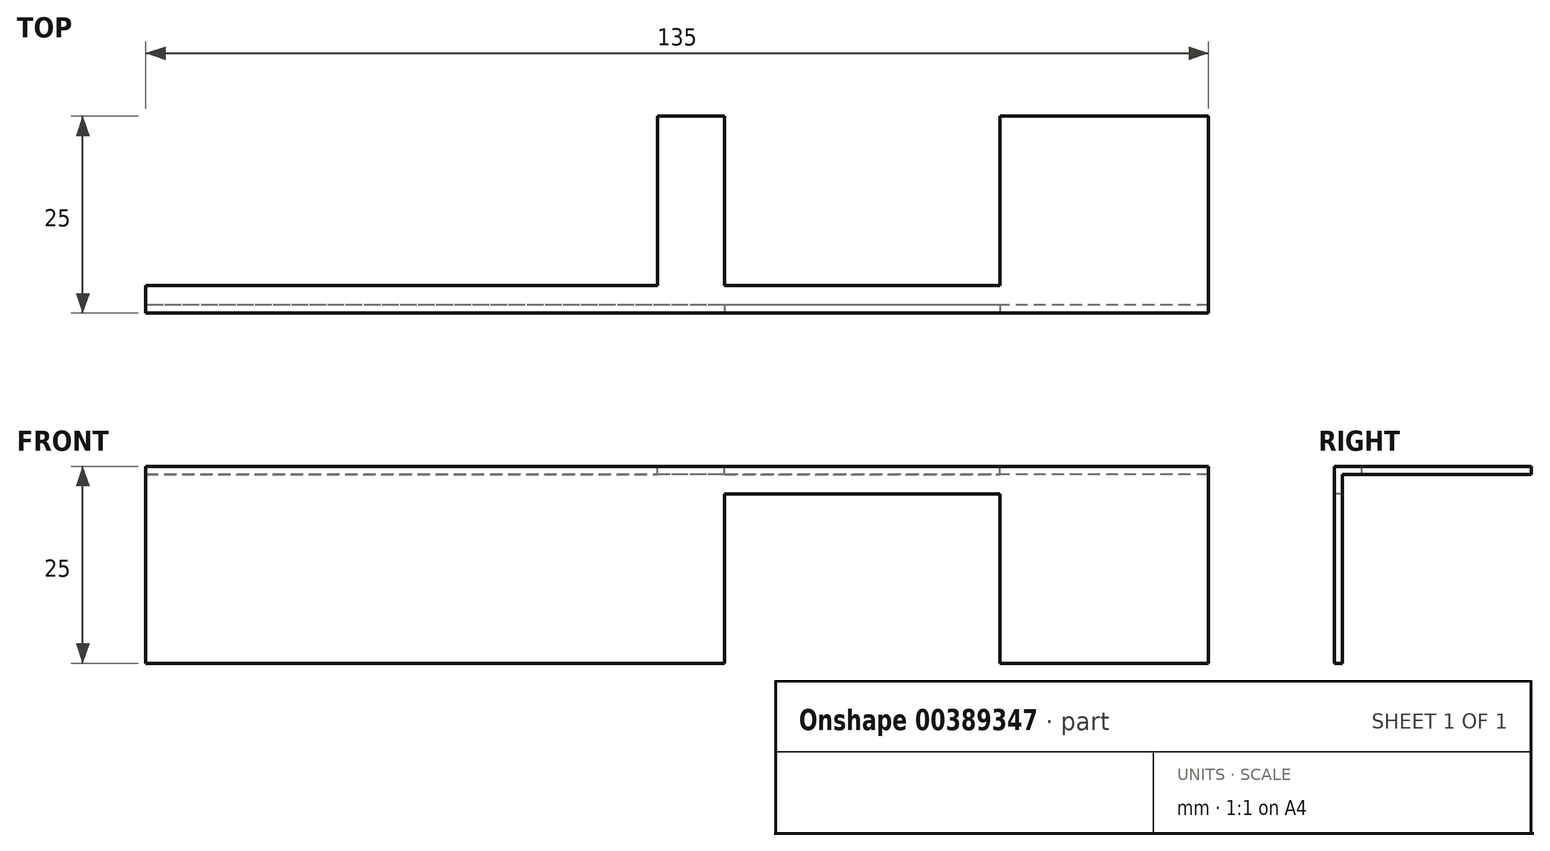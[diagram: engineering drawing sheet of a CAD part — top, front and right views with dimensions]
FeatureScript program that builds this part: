
annotation { "Feature Type Name" : "Feature", "Feature Type Description" : "" }
export const myFeature = defineFeature(function(context is Context, id is Id, definition is map)
    precondition{}
    {
        {
            var Q0;
            Q0=qCreatedBy(makeId("Right.planeOp"),FACE);
            var sketch = newSketch(context, id + "F0", { "sketchPlane" : qUnion([Q0])});
            skLineSegment(sketch, "E0.bottom", {"start": v(-65.04, 19.74) * mm, "end": v(-64.04, 19.74) * mm});
            skLineSegment(sketch, "E0.top", {"start": v(-65.04, 44.74) * mm, "end": v(-64.04, 44.74) * mm});
            skLineSegment(sketch, "E0.left", {"start": v(-65.04, 19.74) * mm, "end": v(-65.04, 44.74) * mm});
            skLineSegment(sketch, "E0.right", {"start": v(-64.04, 19.74) * mm, "end": v(-64.04, 44.74) * mm});
            skLineSegment(sketch, "E1.bottom", {"start": v(-65.04, 44.74) * mm, "end": v(-40.04, 44.74) * mm});
            skLineSegment(sketch, "E1.top", {"start": v(-65.04, 43.74) * mm, "end": v(-40.04, 43.74) * mm});
            skLineSegment(sketch, "E1.left", {"start": v(-65.04, 44.74) * mm, "end": v(-65.04, 43.74) * mm});
            skLineSegment(sketch, "E1.right", {"start": v(-40.04, 44.74) * mm, "end": v(-40.04, 43.74) * mm});
            skSolve(sketch);
        }
        {
            var Q0;
            Q0 = qSketchRegion(id + "F0", true);
            extrude(context, id + "F1", {"entities" : qUnion([Q0]), "depth" : 135 * mm, "offsetDistance" : 25 * mm});
        }
        {
            var Q0;
            Q0=makeQuery(id+"F1.opExtrude","SWEPT_FACE",FACE,{"disambiguationData":[OSD([sQuery(id+"F0.wireOp",EDGE,"E1.bottom")])]});
            var sketch = newSketch(context, id + "F2", { "sketchPlane" : qUnion([Q0])});
            skLineSegment(sketch, "E2.bottom", {"start": v(0, -40.04) * mm, "end": v(65, -40.04) * mm});
            skLineSegment(sketch, "E2.top", {"start": v(0, -61.54) * mm, "end": v(65, -61.54) * mm});
            skLineSegment(sketch, "E2.left", {"start": v(0, -40.04) * mm, "end": v(0, -61.54) * mm});
            skLineSegment(sketch, "E2.right", {"start": v(65, -40.04) * mm, "end": v(65, -61.54) * mm});
            skLineSegment(sketch, "E3.bottom", {"start": v(73.5, -61.54) * mm, "end": v(108.5, -61.54) * mm});
            skLineSegment(sketch, "E3.top", {"start": v(73.5, -40.04) * mm, "end": v(108.5, -40.04) * mm});
            skLineSegment(sketch, "E3.left", {"start": v(73.5, -61.54) * mm, "end": v(73.5, -40.04) * mm});
            skLineSegment(sketch, "E3.right", {"start": v(108.5, -61.54) * mm, "end": v(108.5, -40.04) * mm});
            skSolve(sketch);
        }
        {
            var Q0;
            Q0 = qSketchRegion(id + "F2", true);
            extrude(context, id + "F3", {"entities" : qUnion([Q0]), "operationType" : NewBodyOperationType.REMOVE, "oppositeDirection" : true, "depth" : 1 * mm, "offsetDistance" : 25 * mm});
        }
        {
            var Q0;
            Q0=makeQuery(id+"F1.opExtrude","SWEPT_FACE",FACE,{"disambiguationData":[OSD([sQuery(id+"F0.wireOp",EDGE,"E0.left"),sQuery(id+"F0.wireOp",EDGE,"E1.left")])]});
            var sketch = newSketch(context, id + "F4", { "sketchPlane" : qUnion([Q0])});
            skLineSegment(sketch, "E4.bottom", {"start": v(108.5, 19.74) * mm, "end": v(73.5, 19.74) * mm});
            skLineSegment(sketch, "E4.top", {"start": v(108.5, 41.24) * mm, "end": v(73.5, 41.24) * mm});
            skLineSegment(sketch, "E4.left", {"start": v(108.5, 19.74) * mm, "end": v(108.5, 41.24) * mm});
            skLineSegment(sketch, "E4.right", {"start": v(73.5, 19.74) * mm, "end": v(73.5, 41.24) * mm});
            skSolve(sketch);
        }
        {
            var Q0;
            Q0 = qSketchRegion(id + "F4", true);
            extrude(context, id + "F5", {"entities" : qUnion([Q0]), "operationType" : NewBodyOperationType.REMOVE, "oppositeDirection" : true, "depth" : 1 * mm, "offsetDistance" : 25 * mm});
        }
    });
